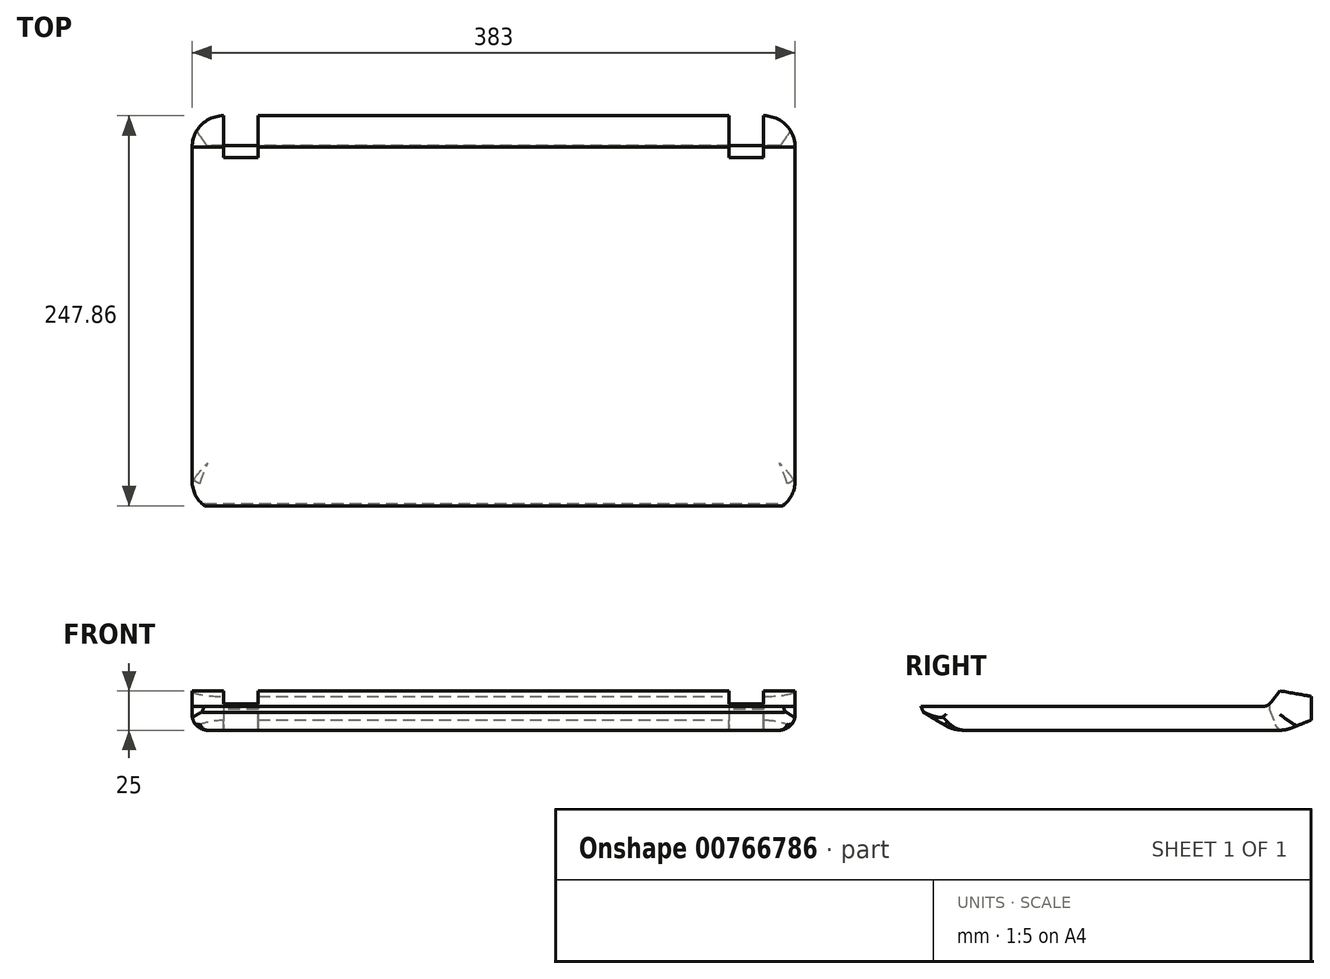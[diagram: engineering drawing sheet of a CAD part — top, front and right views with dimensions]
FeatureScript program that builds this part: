
annotation { "Feature Type Name" : "Feature", "Feature Type Description" : "" }
export const myFeature = defineFeature(function(context is Context, id is Id, definition is map)
    precondition{}
    {
        {
            var Q0;
            Q0=qCreatedBy(makeId("Top.planeOp"),FACE);
            var sketch = newSketch(context, id + "F0", { "sketchPlane" : qUnion([Q0])});
            skLineSegment(sketch, "E0.bottom", {"start": v(171.5, -126) * mm, "end": v(-171.5, -126) * mm});
            skLineSegment(sketch, "E0.top", {"start": v(171.5, 126) * mm, "end": v(-171.5, 126) * mm});
            skLineSegment(sketch, "E0.left", {"start": v(191.5, -106) * mm, "end": v(191.5, 106) * mm});
            skLineSegment(sketch, "E0.right", {"start": v(-191.5, -106) * mm, "end": v(-191.5, 106) * mm});
            skPoint(sketch, "E0.middle", {"position": v(0, 0) * mm});
            skPoint(sketch, "E1.visualSharp", {"position": v(191.5, -126) * mm});
            skArc(sketch, "E1.filletArc", {"start": v(171.5, -126) * mm, "mid": v(185.64, -120.14) * mm, "end": v(191.5, -106) * mm});
            skPoint(sketch, "E2.visualSharp", {"position": v(-191.5, -126) * mm});
            skArc(sketch, "E2.filletArc", {"start": v(-191.5, -106) * mm, "mid": v(-185.64, -120.14) * mm, "end": v(-171.5, -126) * mm});
            skPoint(sketch, "E3.visualSharp", {"position": v(-191.5, 126) * mm});
            skArc(sketch, "E3.filletArc", {"start": v(-171.5, 126) * mm, "mid": v(-185.64, 120.14) * mm, "end": v(-191.5, 106) * mm});
            skPoint(sketch, "E4.visualSharp", {"position": v(191.5, 126) * mm});
            skArc(sketch, "E4.filletArc", {"start": v(191.5, 106) * mm, "mid": v(185.64, 120.14) * mm, "end": v(171.5, 126) * mm});
            skLineSegment(sketch, "E5", {"start": v(-191.47, 107) * mm, "end": v(191.47, 107) * mm});
            skLineSegment(sketch, "E6", {"start": v(-171.5, 126) * mm, "end": v(-171.5, 107) * mm});
            skLineSegment(sketch, "E7", {"start": v(-170.5, 126) * mm, "end": v(-170.5, 107) * mm});
            skLineSegment(sketch, "E8", {"start": v(-150.5, 126) * mm, "end": v(-150.5, 107) * mm});
            skLineSegment(sketch, "E9", {"start": v(-149.5, 126) * mm, "end": v(-149.5, 107) * mm});
            skLineSegment(sketch, "E10", {"start": v(149.5, 126) * mm, "end": v(149.5, 107) * mm});
            skLineSegment(sketch, "E11", {"start": v(150.5, 126) * mm, "end": v(150.5, 107) * mm});
            skLineSegment(sketch, "E12", {"start": v(170.5, 126) * mm, "end": v(170.5, 107) * mm});
            skLineSegment(sketch, "E13", {"start": v(171.5, 126) * mm, "end": v(171.5, 107) * mm});
            skLineSegment(sketch, "E14", {"start": v(-171.5, 107) * mm, "end": v(-171.5, 99.5) * mm});
            skLineSegment(sketch, "E15", {"start": v(-171.5, 99.5) * mm, "end": v(-149.5, 99.5) * mm});
            skLineSegment(sketch, "E16", {"start": v(-149.5, 99.5) * mm, "end": v(-149.5, 107) * mm});
            skLineSegment(sketch, "E17", {"start": v(149.5, 107) * mm, "end": v(149.5, 99.5) * mm});
            skLineSegment(sketch, "E18", {"start": v(149.5, 99.5) * mm, "end": v(171.5, 99.5) * mm});
            skLineSegment(sketch, "E19", {"start": v(171.5, 99.5) * mm, "end": v(171.5, 107) * mm});
            skSolve(sketch);
        }
        {
            var Q0;
            Q0=makeQuery(id+"F0.imprint","IMPRINT",FACE,{"disambiguationData":[TD([[makeQuery(id+"F0.imprint","IMPRINT",EDGE,{"derivedFrom":sQuery(id+"F0.wireOp",EDGE,"E0.bottom")}),-1.0]])]});
            var Q1;
            {var subQ0=sQuery(id+"F0.wireOp",EDGE,"E9");Q1=makeQuery(id+"F0.imprint","IMPRINT",FACE,{"disambiguationData":[TD([[makeQuery(id+"F0.imprint","IMPRINT",EDGE,{"derivedFrom":subQ0}),1.0]])]});}
            var Q2;
            {var subQ0=sQuery(id+"F0.wireOp",EDGE,"E13");Q2=makeQuery(id+"F0.imprint","IMPRINT",FACE,{"disambiguationData":[TD([[makeQuery(id+"F0.imprint","IMPRINT",EDGE,{"derivedFrom":subQ0}),1.0]])]});}
            var Q3;
            {var subQ0=sQuery(id+"F0.wireOp",EDGE,"E6");Q3=makeQuery(id+"F0.imprint","IMPRINT",FACE,{"disambiguationData":[TD([[makeQuery(id+"F0.imprint","IMPRINT",EDGE,{"derivedFrom":subQ0}),-1.0]])]});}
            extrude(context, id + "F1", {"entities" : qUnion([Q0, Q1, Q2, Q3]), "depth" : 25 * mm, "offsetDistance" : 25 * mm});
        }
        {
            var Q0;
            Q0=qCreatedBy(makeId("Right.planeOp"),FACE);
            var sketch = newSketch(context, id + "F2", { "sketchPlane" : qUnion([Q0])});
            skLineSegment(sketch, "E20", {"start": v(-121.86, 15) * mm, "end": v(94.63, 15) * mm});
            skLineSegment(sketch, "E21", {"start": v(-121.86, 15) * mm, "end": v(-120.33, 11.3) * mm});
            skLineSegment(sketch, "E22", {"start": v(-120.33, 11.3) * mm, "end": v(-107.47, 3.57) * mm});
            skLineSegment(sketch, "E23", {"start": v(-94.59, 0) * mm, "end": v(106, 0) * mm});
            skLineSegment(sketch, "E24", {"start": v(-121.86, 15) * mm, "end": v(-121.86, 25) * mm});
            skLineSegment(sketch, "E25", {"start": v(-121.86, 25) * mm, "end": v(126, 25) * mm});
            skLineSegment(sketch, "E26", {"start": v(113.45, 1.44) * mm, "end": v(126, 6.47) * mm});
            skLineSegment(sketch, "E27", {"start": v(126, 6.47) * mm, "end": v(126, 21.47) * mm});
            skLineSegment(sketch, "E28", {"start": v(-121.86, 17) * mm, "end": v(93.64, 17) * mm});
            skLineSegment(sketch, "E29", {"start": v(106, 0) * mm, "end": v(106, 25) * mm});
            skPoint(sketch, "E30.visualSharp", {"position": v(-101.53, 0) * mm});
            skArc(sketch, "E30.filletArc", {"start": v(-107.47, 3.57) * mm, "mid": v(-101.27, 0.91) * mm, "end": v(-94.59, 0) * mm});
            skLineSegment(sketch, "E31", {"start": v(126, 21.47) * mm, "end": v(126, 25) * mm});
            skLineSegment(sketch, "E32", {"start": v(126, 6.47) * mm, "end": v(126, 0) * mm});
            skLineSegment(sketch, "E33", {"start": v(-121.86, 15) * mm, "end": v(-121.86, 0) * mm});
            skLineSegment(sketch, "E34", {"start": v(-121.86, 0) * mm, "end": v(-94.59, 0) * mm});
            skLineSegment(sketch, "E35", {"start": v(106, 25) * mm, "end": v(126, 21.47) * mm});
            skLineSegment(sketch, "E36", {"start": v(100.58, 17.93) * mm, "end": v(106, 25) * mm});
            skLineSegment(sketch, "E37", {"start": v(99.6, 19.93) * mm, "end": v(103.48, 25) * mm});
            skArc(sketch, "E38.filletArc", {"start": v(93.64, 17) * mm, "mid": v(96.96, 17.77) * mm, "end": v(99.6, 19.93) * mm});
            skArc(sketch, "E39.filletArc", {"start": v(94.63, 15) * mm, "mid": v(97.95, 15.77) * mm, "end": v(100.58, 17.93) * mm});
            skArc(sketch, "E40.filletArc", {"start": v(106, 0) * mm, "mid": v(109.8, 0.36) * mm, "end": v(113.45, 1.44) * mm});
            skLineSegment(sketch, "E41", {"start": v(-121.86, 25) * mm, "end": v(-126, 25) * mm});
            skLineSegment(sketch, "E42", {"start": v(-126, 25) * mm, "end": v(-126, 0) * mm});
            skLineSegment(sketch, "E43", {"start": v(-126, 0) * mm, "end": v(-121.86, 0) * mm});
            skLineSegment(sketch, "E44", {"start": v(-126, 25) * mm, "end": v(-121.86, 15) * mm});
            skLineSegment(sketch, "E45", {"start": v(106, 0) * mm, "end": v(126, 0) * mm});
            skSolve(sketch);
        }
        {
            var Q0;
            {var subQ1=sQuery(id+"F2.wireOp",EDGE,"E28");Q0=makeQuery(id+"F2.imprint","IMPRINT",FACE,{"disambiguationData":[TD([[makeQuery(id+"F2.imprint","IMPRINT",EDGE,{"derivedFrom":subQ1}),1.0]])]});}
            var Q1;
            {var subQ5=sQuery(id+"F2.wireOp",EDGE,"E20");Q1=makeQuery(id+"F2.imprint","IMPRINT",FACE,{"disambiguationData":[TD([[makeQuery(id+"F2.imprint","IMPRINT",EDGE,{"derivedFrom":subQ5}),1.0]])]});}
            var Q2;
            {var subQ0=sQuery(id+"F2.wireOp",EDGE,"E31");Q2=makeQuery(id+"F2.imprint","IMPRINT",FACE,{"disambiguationData":[TD([[makeQuery(id+"F2.imprint","IMPRINT",EDGE,{"derivedFrom":subQ0}),1.0]])]});}
            var Q3;
            Q3=makeQuery(id+"F2.imprint","IMPRINT",FACE,{"disambiguationData":[TD([[makeQuery(id+"F2.imprint","IMPRINT",EDGE,{"derivedFrom":sQuery(id+"F2.wireOp",EDGE,"E26")}),-1.0]])]});
            var Q4;
            Q4=makeQuery(id+"F2.imprint","IMPRINT",FACE,{"disambiguationData":[TD([[makeQuery(id+"F2.imprint","IMPRINT",EDGE,{"derivedFrom":sQuery(id+"F2.wireOp",EDGE,"E21")}),-1.0]])]});
            var Q5;
            {var subQ3=sQuery(id+"F2.wireOp",EDGE,"E41");Q5=makeQuery(id+"F2.imprint","IMPRINT",FACE,{"disambiguationData":[TD([[makeQuery(id+"F2.imprint","IMPRINT",EDGE,{"derivedFrom":subQ3}),1.0]])]});}
            var Q6;
            Q6=makeQuery(id+"F2.imprint","IMPRINT",FACE,{"disambiguationData":[TD([[makeQuery(id+"F2.imprint","IMPRINT",EDGE,{"derivedFrom":sQuery(id+"F2.wireOp",EDGE,"E33")}),-1.0]])]});
            var Q7;
            Q7=sQuery(id+"F2.wireOp",EDGE,"E22");
            var Q8;
            Q8=sQuery(id+"F2.wireOp",EDGE,"E21");
            var Q9;
            Q9=sQuery(id+"F2.wireOp",EDGE,"E20");
            var Q10;
            Q10=sQuery(id+"F2.wireOp",EDGE,"E30.filletArc");
            var Q11;
            Q11=sQuery(id+"F2.wireOp",EDGE,"E23");
            var Q12;
            Q12=sQuery(id+"F2.wireOp",EDGE,"e3037af8-f494-44ef-9f05-5a72e9663ddf.filletArc");
            var Q13;
            Q13=sQuery(id+"F2.wireOp",EDGE,"eUjnkxIL-uigh-wOqe-7D7o-ZUrcahEpG87n");
            var Q14;
            Q14=sQuery(id+"F2.wireOp",EDGE,"m5Z8WM2A-77N3-vOnY-M6bB-hViUhZig5UtK");
            var Q15;
            Q15=sQuery(id+"F2.wireOp",EDGE,"E27");
            var Q16;
            Q16=sQuery(id+"F2.wireOp",EDGE,"E26");
            var Q17;
            Q17=sQuery(id+"F2.wireOp",EDGE,"c018d4ad-c3dc-471c-9e16-3ae35aacb8e4.filletArc");
            extrude(context, id + "F3", {"entities" : qUnion([Q0, Q1, Q2, Q3, Q4, Q5, Q6]), "operationType" : NewBodyOperationType.REMOVE, "surfaceEntities" : qUnion([Q7, Q8, Q9, Q10, Q11, Q12, Q13, Q14, Q15, Q16, Q17]), "oppositeDirection" : true, "depth" : 383 * mm, "offsetDistance" : 25 * mm, "symmetric" : true});
        }
        {
            var Q0;
            Q0=qCreatedBy(makeId("Right.planeOp"),FACE);
            var sketch = newSketch(context, id + "F4", { "sketchPlane" : qUnion([Q0])});
            skLineSegment(sketch, "E46", {"start": v(107, 0) * mm, "end": v(105.18, 1.07) * mm});
            skLineSegment(sketch, "E47", {"start": v(103.02, 3.67) * mm, "end": v(98.5, 16.08) * mm});
            skLineSegment(sketch, "E48", {"start": v(98.5, 16.08) * mm, "end": v(98.5, 0) * mm});
            skLineSegment(sketch, "E49", {"start": v(98.5, 0) * mm, "end": v(107, 0) * mm});
            skPoint(sketch, "E50.visualSharp", {"position": v(103.63, 1.98) * mm});
            skArc(sketch, "E50.filletArc", {"start": v(103.02, 3.67) * mm, "mid": v(103.87, 2.18) * mm, "end": v(105.18, 1.07) * mm});
            skSolve(sketch);
        }
        {
            var Q0;
            Q0 = qSketchRegion(id + "F4", true);
            extrude(context, id + "F5", {"entities" : qUnion([Q0]), "operationType" : NewBodyOperationType.ADD, "depth" : 383 * mm, "offsetDistance" : 25 * mm, "symmetric" : true});
        }
        {
            var Q0;
            Q0=qCreatedBy(makeId("Front.planeOp"),FACE);
            var sketch = newSketch(context, id + "F6", { "sketchPlane" : qUnion([Q0])});
            skLineSegment(sketch, "E51.bottom", {"start": v(-191.5, 25) * mm, "end": v(191.5, 25) * mm});
            skLineSegment(sketch, "E51.top", {"start": v(-181.5, 0) * mm, "end": v(181.5, 0) * mm});
            skLineSegment(sketch, "E51.left", {"start": v(-191.5, 25) * mm, "end": v(-191.5, 10) * mm});
            skLineSegment(sketch, "E51.right", {"start": v(191.5, 25) * mm, "end": v(191.5, 10) * mm});
            skPoint(sketch, "E52.visualSharp", {"position": v(-191.5, 0) * mm});
            skArc(sketch, "E52.filletArc", {"start": v(-191.5, 10) * mm, "mid": v(-188.57, 2.93) * mm, "end": v(-181.5, 0) * mm});
            skPoint(sketch, "E53.visualSharp", {"position": v(191.5, 0) * mm});
            skArc(sketch, "E53.filletArc", {"start": v(181.5, 0) * mm, "mid": v(188.57, 2.93) * mm, "end": v(191.5, 10) * mm});
            skLineSegment(sketch, "E54", {"start": v(-191.5, 0) * mm, "end": v(-181.5, 0) * mm});
            skLineSegment(sketch, "E55", {"start": v(-191.5, 0) * mm, "end": v(-191.5, 10) * mm});
            skLineSegment(sketch, "E56", {"start": v(181.5, 0) * mm, "end": v(191.5, 0) * mm});
            skLineSegment(sketch, "E57", {"start": v(191.5, 0) * mm, "end": v(191.5, 10) * mm});
            skSolve(sketch);
        }
        {
            var Q0;
            Q0=makeQuery(id+"F6.imprint","IMPRINT",FACE,{"disambiguationData":[TD([[makeQuery(id+"F6.imprint","IMPRINT",EDGE,{"derivedFrom":sQuery(id+"F6.wireOp",EDGE,"E52.filletArc")}),-1.0]])]});
            var Q1;
            Q1=makeQuery(id+"F6.imprint","IMPRINT",FACE,{"disambiguationData":[TD([[makeQuery(id+"F6.imprint","IMPRINT",EDGE,{"derivedFrom":sQuery(id+"F6.wireOp",EDGE,"E53.filletArc")}),-1.0]])]});
            extrude(context, id + "F7", {"entities" : qUnion([Q0, Q1]), "operationType" : NewBodyOperationType.REMOVE, "depth" : 262 * mm, "offsetDistance" : 25 * mm, "symmetric" : true});
        }
        {
            var Q0;
            Q0=makeQuery(id+"F7.boolean.opBoolean","INTERSECT",EDGE,{"derivedFrom":[makeQuery(id+"F3.boolean.opBoolean","COPY",FACE,{"derivedFrom":makeQuery(id+"F3.opExtrude","SWEPT_FACE",FACE,{"disambiguationData":[OSD([sQuery(id+"F2.wireOp",EDGE,"E30.filletArc")])]})}),makeQuery(id+"F7.opExtrude","SWEPT_FACE",FACE,{"disambiguationData":[OSD([sQuery(id+"F6.wireOp",EDGE,"E52.filletArc")])]})]});
            var Q1;
            Q1=makeQuery(id+"F7.boolean.opBoolean","INTERSECT",EDGE,{"derivedFrom":[makeQuery(id+"F3.boolean.opBoolean","COPY",FACE,{"derivedFrom":makeQuery(id+"F3.opExtrude","SWEPT_FACE",FACE,{"disambiguationData":[OSD([sQuery(id+"F2.wireOp",EDGE,"E30.filletArc")])]})}),makeQuery(id+"F7.opExtrude","SWEPT_FACE",FACE,{"disambiguationData":[OSD([sQuery(id+"F6.wireOp",EDGE,"E53.filletArc")])]})]});
            var Q2;
            Q2=makeQuery(id+"F7.boolean.opBoolean","INTERSECT",EDGE,{"derivedFrom":[makeQuery(id+"F3.boolean.opBoolean","COPY",FACE,{"derivedFrom":makeQuery(id+"F3.opExtrude","SWEPT_FACE",FACE,{"disambiguationData":[OSD([sQuery(id+"F2.wireOp",EDGE,"E22")])]})}),makeQuery(id+"F7.opExtrude","SWEPT_FACE",FACE,{"disambiguationData":[OSD([sQuery(id+"F6.wireOp",EDGE,"E52.filletArc")])]})]});
            var Q3;
            Q3=makeQuery(id+"F7.boolean.opBoolean","INTERSECT",EDGE,{"derivedFrom":[makeQuery(id+"F3.boolean.opBoolean","COPY",FACE,{"derivedFrom":makeQuery(id+"F3.opExtrude","SWEPT_FACE",FACE,{"disambiguationData":[OSD([sQuery(id+"F2.wireOp",EDGE,"E22")])]})}),makeQuery(id+"F7.opExtrude","SWEPT_FACE",FACE,{"disambiguationData":[OSD([sQuery(id+"F6.wireOp",EDGE,"E53.filletArc")])]})]});
            fillet(context, id + "F8", {"entities" : qUnion([Q0, Q1, Q2, Q3]), "tangentPropagation" : true, "radius" : 4.5 * mm, "defaultsChanged" : true, "vertexSettings" : [], "allowEdgeOverflow" : false});
        }
    });
